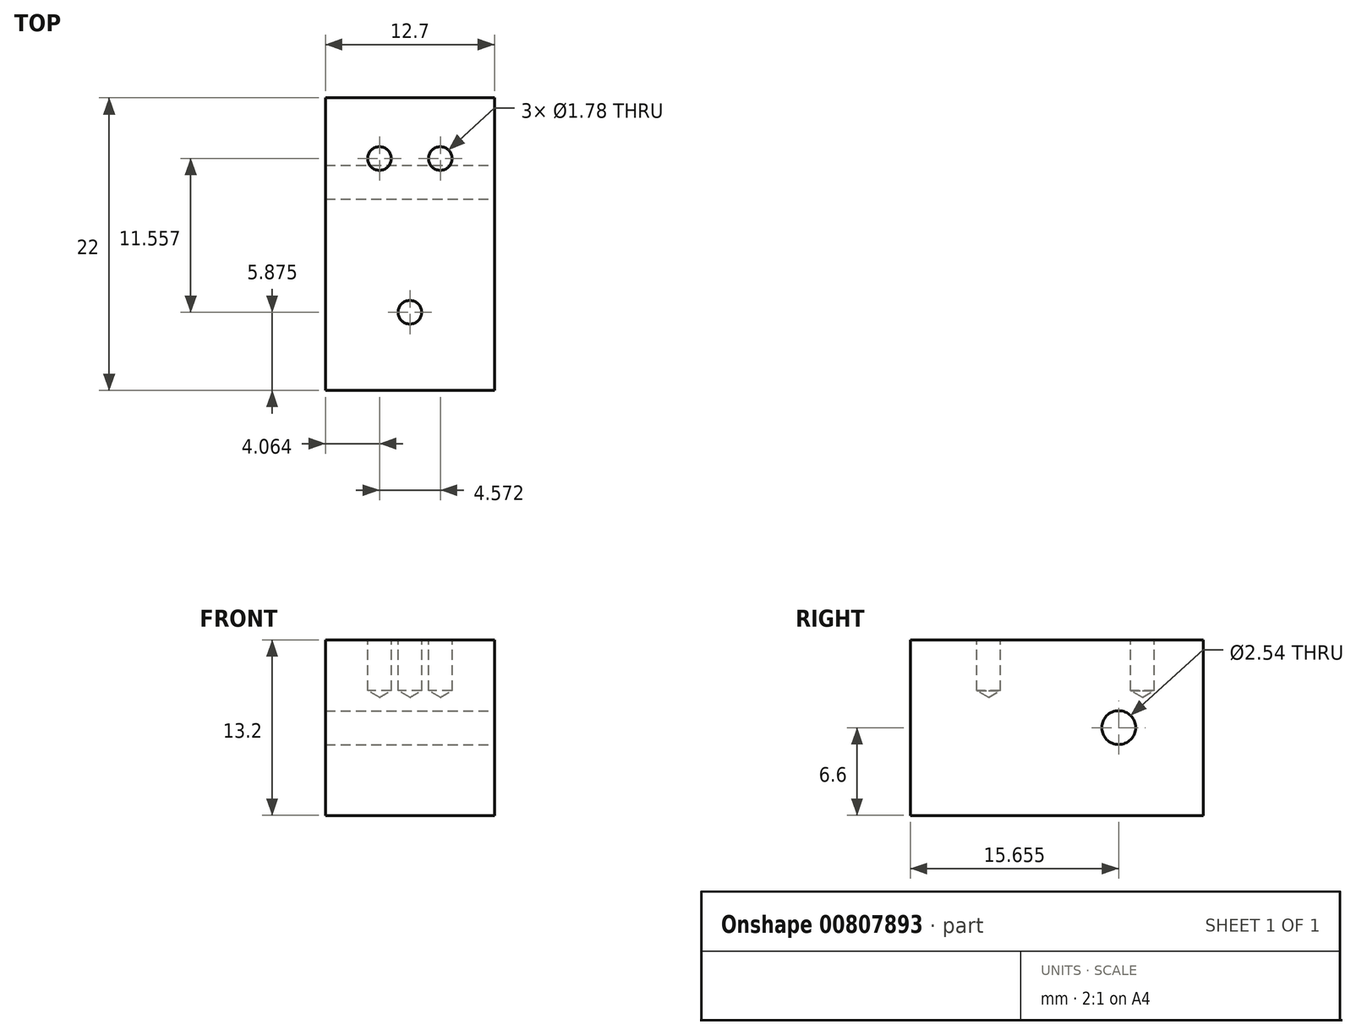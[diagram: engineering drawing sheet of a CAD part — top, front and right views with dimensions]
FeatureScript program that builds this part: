
annotation { "Feature Type Name" : "Feature", "Feature Type Description" : "" }
export const myFeature = defineFeature(function(context is Context, id is Id, definition is map)
    precondition{}
    {
        {
            var Q0;
            Q0=qCreatedBy(makeId("Top.planeOp"),FACE);
            var sketch = newSketch(context, id + "F0", { "sketchPlane" : qUnion([Q0])});
            skLineSegment(sketch, "E0.bottom", {"start": v(-6.35, 11) * mm, "end": v(6.35, 11) * mm});
            skLineSegment(sketch, "E0.top", {"start": v(-6.35, -11) * mm, "end": v(6.35, -11) * mm});
            skLineSegment(sketch, "E0.left", {"start": v(-6.35, 11) * mm, "end": v(-6.35, -11) * mm});
            skLineSegment(sketch, "E0.right", {"start": v(6.35, 11) * mm, "end": v(6.35, -11) * mm});
            skLineSegment(sketch, "E1", {"start": v(-6.35, -11) * mm, "end": v(6.35, 11) * mm, "construction": true});
            skSolve(sketch);
        }
        {
            var Q0;
            Q0 = qSketchRegion(id + "F0", true);
            extrude(context, id + "F1", {"entities" : qUnion([Q0]), "endBound" : BoundingType.SYMMETRIC, "depth" : 13.2 * mm, "offsetDistance" : 25.4 * mm});
        }
        {
            var Q0;
            Q0=makeQuery(id+"F1.opExtrude","SWEPT_FACE",FACE,{"disambiguationData":[OSD([sQuery(id+"F0.wireOp",EDGE,"E0.right")])]});
            var sketch = newSketch(context, id + "F2", { "sketchPlane" : qUnion([Q0])});
            skCircle(sketch, "E2", {"center": v(4.65, 0) * mm, "radius": 1.27 * mm});
            skSolve(sketch);
        }
        {
            var Q0;
            Q0 = qSketchRegion(id + "F2", true);
            extrude(context, id + "F3", {"entities" : qUnion([Q0]), "operationType" : NewBodyOperationType.REMOVE, "endBound" : BoundingType.THROUGH_ALL, "oppositeDirection" : true, "depth" : 25.4 * mm, "offsetDistance" : 25.4 * mm});
        }
        {
            var Q0;
            Q0=makeQuery(id+"F1.opExtrude","CAP_FACE",FACE,{"disambiguationData":[OSD([sQuery(id+"F0.wireOp",EDGE,"E0.bottom"),sQuery(id+"F0.wireOp",EDGE,"E0.top"),sQuery(id+"F0.wireOp",EDGE,"E0.left"),sQuery(id+"F0.wireOp",EDGE,"E0.right")])],"isStart":false});
            var sketch = newSketch(context, id + "F4", { "sketchPlane" : qUnion([Q0])});
            skPoint(sketch, "E3", {"position": v(-2.29, 6.43) * mm});
            skPoint(sketch, "E4", {"position": v(2.29, 6.43) * mm});
            skPoint(sketch, "E5", {"position": v(0, -5.12) * mm});
            skSolve(sketch);
        }
        {
            var Q0;
            Q0=sQuery(id+"F4.wireOp",VERTEX,"E3");
            var Q1;
            Q1=sQuery(id+"F4.wireOp",VERTEX,"E4");
            var Q2;
            Q2=sQuery(id+"F4.wireOp",VERTEX,"E5");
            var Q3;
            Q3=makeQuery(id+"F1.opExtrude","SWEPT_BODY",BODY,{"disambiguationData":[OSD([sQuery(id+"F0.wireOp",EDGE,"E0.bottom"),sQuery(id+"F0.wireOp",EDGE,"E0.top"),sQuery(id+"F0.wireOp",EDGE,"E0.left"),sQuery(id+"F0.wireOp",EDGE,"E0.right")])]});
            hole(context, id + "F5", {"style" : HoleStyle.SIMPLE, "endStyle" : HoleEndStyle.BLIND, "standardTappedOrClearance" : lookupTablePath({ "standard" : "ANSI", "engagement" : "75%", "pitch" : "56 tpi", "size" : "#2", "type" : "Tapped" }), "standardBlindInLast" : lookupTablePath({ "standard" : "ANSI", "engagement" : "75%", "pitch" : "56 tpi", "size" : "#2", "type" : "Tapped" }), "holeDiameter" : 1.78 * mm, "majorDiameter" : 2.18 * mm, "showTappedDepth" : true, "holeDepth" : 3.8 * mm, "tappedDepth" : 2.45 * mm, "tapClearance" : 3, "locations" : qUnion([Q0, Q1, Q2]), "scope" : qUnion([Q3])});
        }
    });
